# Revit family: CRIG-3558
name_source: partatom
category: Lighting Fixtures
units: mm (PartAtom-declared; Revit-internal decimal feet)

## family parameters
Always vertical = Yes
Cut with Voids When Loaded = No
Host = Ceiling
Light Source = Yes
OmniClass Number = 23.80.70.11
OmniClass Title = Luminaries for Internal Lighting
Part Type = Normal
Room Calculation Point = No
Round Connector Dimension = Use Diameter
Shared = No

## types (8) — shared parameters
Assembly Code = D5020200
Color Filter = 16777215
Description = Recessed Grid Inset Door Cleanroom LED Luminaire
Dimming Lamp Color Temperature Shift = <None>
Emit Shape Visible in Rendering = No
Housing Finish = Metal - Viscor - White
Lamp = LED
Lens Finish = Polycarbonate - Viscor - Frosted Flat
Manufacturer = CERTOLUX by VISCOR
Model = CRIG-3558
Tilt Angle = 90.00°
URL = https://www.viscor.com
Voltage = 120 V

## per-type parameters (varying)
| type | Apparent Load | Emit from Rectangle Length | Emit from Rectangle Width | Lamp Wattage | Length | Photometric Web File | Width |
| CRIG-3558-1X4-LED840K52LUNV-P13 | 50 VA | 3' - 11 3/4" | 0' - 11 3/4" | 50 VA | 3' - 11 3/4" | CRIG-3558-1x4-LED840K52LUNV-P13.ies | 0' - 11 3/4" |
| CRIG-3558-2X4-LED840K78LUNV-P13 | 75 VA | 3' - 11 3/4" | 1' - 11 3/4" | 75 VA | 3' - 11 3/4" | CRIG-3558-2X4-LED840K78LUNV-P13.ies | 1' - 11 3/4" |
| CRIG-3558-2X2-LED840K35LUNV-P13 | 32 VA | 1' - 11 3/4" | 1' - 11 3/4" | 32 VA | 1' - 11 3/4" | CRIG-3558-2x2-LED840K35LUNV-P13.ies | 1' - 11 3/4" |
| CRIG-3558-2X2-LED835K26LUNV-P13 | 27 VA | 1' - 11 3/4" | 1' - 11 3/4" | 27 VA | 1' - 11 3/4" | CRIG-3558-2X2-LED835K26LUNV-P13.ies | 1' - 11 3/4" |
| CRIG-3558-2x2-LED840K52LUNV-P13 | 48 VA | 1' - 11 3/4" | 1' - 11 3/4" | 48 VA | 1' - 11 3/4" | CRIG-3558-2x2-LED840K52LUNV-P13.ies | 1' - 11 3/4" |
| CRIG-3558-2X2-LED840K66LUNV-P56 | 61 VA | 1' - 11 3/4" | 1' - 11 3/4" | 61 VA | 1' - 11 3/4" | CRIG-3558-2X2-LED840K66LUNV-P56.ies | 1' - 11 3/4" |
| CRIG-3558-2X4-LED840K52LUNV-P13 | 49 VA | 3' - 11 3/4" | 1' - 11 3/4" | 49 VA | 3' - 11 3/4" | CRIG-3558-2X4-LED840K52LUNV-P13.ies | 1' - 11 3/4" |
| CRIG-3558-2X4-LED840K104LUNV-P82 | 98 VA | 3' - 11 3/4" | 1' - 11 3/4" | 98 VA | 3' - 11 3/4" | CRIG-3558-2X4-LED840K104LUNV-P82.ies | 1' - 11 3/4" |

## geometry (parser evidence)
native form markers: Sweep x1
no freeform markers — native parametric forms only
